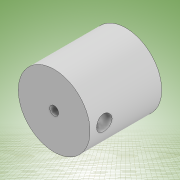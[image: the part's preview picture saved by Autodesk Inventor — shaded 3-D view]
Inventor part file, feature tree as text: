
AUTODESK INVENTOR PART (.ipt)
format: ipt  version: 2022 (Build 260153000, 153)  size: 147,456 bytes
history: native  units: mm
features: sketch x4, extrude x3, other x1, plane x1, hole x1
ambient origin geometry x8: Origin, YZ Plane, XZ Plane, XY Plane, X Axis, Y Axis, Z Axis, Center Point
bodies: Body1 (feature_tree)
feature tree (10):
  other  "Sólido1"
  extrude  "Extrusión1"  Depth=20.0mm TaperAngle=0.0deg
  extrude  "Extrusión2"  Depth=10.0mm TaperAngle=0.0deg
  extrude  "Extrusión3"  Depth=10.0mm TaperAngle=0.0deg
  plane  "Plano de trabajo1"
  hole  "Agujero1"  [1 undecoded]
  sketch  "Boceto1"  dims[d0=20.0mm d1=20.0mm d2=0.0mm]
  sketch  "Boceto2"  dims[d3=2.5mm d4=10.0mm d5=0.0mm]
  sketch  "Boceto3"  dims[d6=6.1mm d7=10.0mm d8=0.0mm]
  sketch  "Boceto4"  dims[d11=4.0mm d12=4.0mm d13=4.3mm d14=6.0mm d15=4.0mm d16=2.0mm d17=90.0deg d18=8.0mm d19=20.594885mm]
note: 1 required parameter value undecoded (feature->parameter linkage not recoverable at this tier; creation-order binding heuristic only, values carry confidence <= 0.55)
